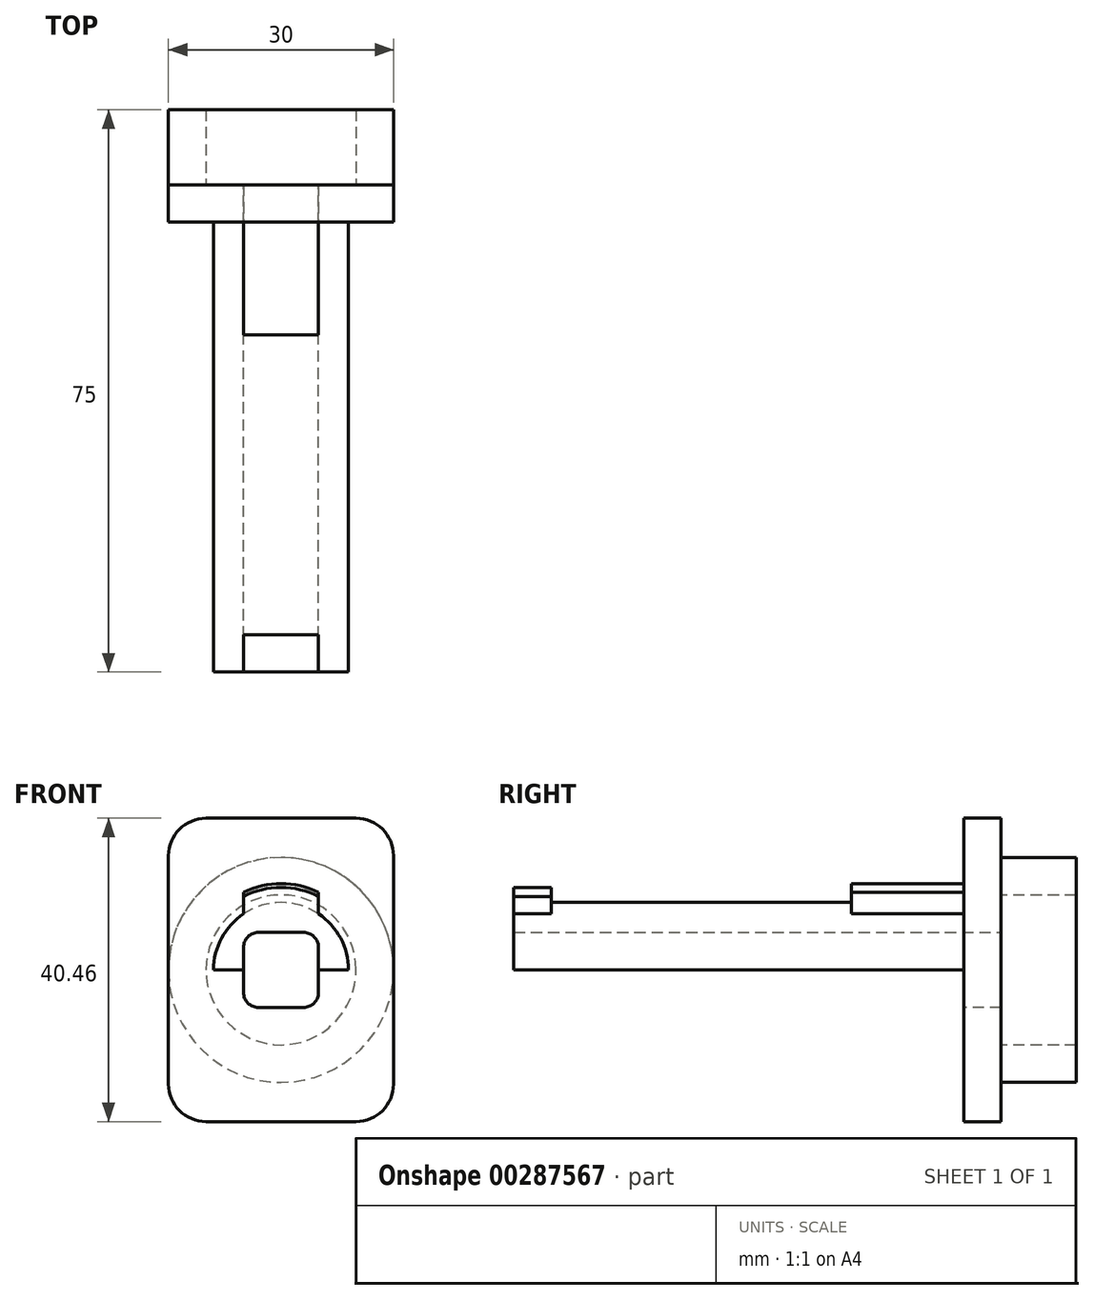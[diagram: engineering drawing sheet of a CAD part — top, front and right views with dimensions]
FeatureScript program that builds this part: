
annotation { "Feature Type Name" : "Feature", "Feature Type Description" : "" }
export const myFeature = defineFeature(function(context is Context, id is Id, definition is map)
    precondition{}
    {
        {
            var Q0;
            Q0=qCreatedBy(makeId("Front.planeOp"),FACE);
            var sketch = newSketch(context, id + "F0", { "sketchPlane" : qUnion([Q0])});
            skArc(sketch, "E0", {"start": v(9, 0) * mm, "mid": v(0, 9) * mm, "end": v(-9, 0) * mm});
            skLineSegment(sketch, "E1.bottom", {"start": v(10, -20.23) * mm, "end": v(-10, -20.23) * mm});
            skLineSegment(sketch, "E1.top", {"start": v(10, 20.23) * mm, "end": v(-10, 20.23) * mm});
            skLineSegment(sketch, "E1.left", {"start": v(15, -15.23) * mm, "end": v(15, 15.23) * mm});
            skLineSegment(sketch, "E1.right", {"start": v(-15, -15.23) * mm, "end": v(-15, 15.23) * mm});
            skPoint(sketch, "E2.visualSharp", {"position": v(-15, 20.23) * mm});
            skArc(sketch, "E2.filletArc", {"start": v(-10, 20.23) * mm, "mid": v(-13.54, 18.77) * mm, "end": v(-15, 15.23) * mm});
            skPoint(sketch, "E3.visualSharp", {"position": v(15, 20.23) * mm});
            skArc(sketch, "E3.filletArc", {"start": v(15, 15.23) * mm, "mid": v(13.54, 18.77) * mm, "end": v(10, 20.23) * mm});
            skPoint(sketch, "E4.visualSharp", {"position": v(15, -20.23) * mm});
            skArc(sketch, "E4.filletArc", {"start": v(10, -20.23) * mm, "mid": v(13.54, -18.77) * mm, "end": v(15, -15.23) * mm});
            skPoint(sketch, "E5.visualSharp", {"position": v(-15, -20.23) * mm});
            skArc(sketch, "E5.filletArc", {"start": v(-15, -15.23) * mm, "mid": v(-13.54, -18.77) * mm, "end": v(-10, -20.23) * mm});
            skLineSegment(sketch, "E6", {"start": v(-9, 0) * mm, "end": v(9, 0) * mm});
            skLineSegment(sketch, "E7.bottom", {"start": v(3, 5) * mm, "end": v(-3, 5) * mm});
            skLineSegment(sketch, "E7.top", {"start": v(3, -5) * mm, "end": v(-3, -5) * mm});
            skLineSegment(sketch, "E7.left", {"start": v(5, 3) * mm, "end": v(5, -3) * mm});
            skLineSegment(sketch, "E7.right", {"start": v(-5, 3) * mm, "end": v(-5, -3) * mm});
            skPoint(sketch, "E8.visualSharp", {"position": v(-5, 5) * mm});
            skArc(sketch, "E8.filletArc", {"start": v(-3, 5) * mm, "mid": v(-4.41, 4.41) * mm, "end": v(-5, 3) * mm});
            skPoint(sketch, "E9.visualSharp", {"position": v(5, 5) * mm});
            skArc(sketch, "E9.filletArc", {"start": v(5, 3) * mm, "mid": v(4.41, 4.41) * mm, "end": v(3, 5) * mm});
            skPoint(sketch, "E10.visualSharp", {"position": v(-5, -5) * mm});
            skArc(sketch, "E10.filletArc", {"start": v(-5, -3) * mm, "mid": v(-4.41, -4.41) * mm, "end": v(-3, -5) * mm});
            skPoint(sketch, "E11.visualSharp", {"position": v(5, -5) * mm});
            skArc(sketch, "E11.filletArc", {"start": v(3, -5) * mm, "mid": v(4.41, -4.41) * mm, "end": v(5, -3) * mm});
            skArc(sketch, "E12", {"start": v(5, 10.36) * mm, "mid": v(0, 11.5) * mm, "end": v(-5, 10.36) * mm});
            skLineSegment(sketch, "E13", {"start": v(-5, 3) * mm, "end": v(-5, 10.36) * mm});
            skLineSegment(sketch, "E14", {"start": v(5, 3) * mm, "end": v(5, 10.36) * mm});
            skSolve(sketch);
        }
        {
            var Q0;
            Q0=makeQuery(id+"F0.imprint","IMPRINT",FACE,{"disambiguationData":[TD([[makeQuery(id+"F0.imprint","IMPRINT",EDGE,{"derivedFrom":sQuery(id+"F0.wireOp",EDGE,"E0")}),1.0]])]});
            var Q1;
            Q1=makeQuery(id+"F0.imprint","IMPRINT",FACE,{"disambiguationData":[TD([[makeQuery(id+"F0.imprint","IMPRINT",EDGE,{"derivedFrom":sQuery(id+"F0.wireOp",EDGE,"E7.bottom")}),-1.0]])]});
            extrude(context, id + "F1", {"entities" : qUnion([Q0, Q1]), "depth" : 55 * mm});
        }
        {
            var Q0;
            Q0=makeQuery(id+"F1.opExtrude","CAP_FACE",FACE,{"disambiguationData":[OSD([sQuery(id+"F0.wireOp",EDGE,"E0"),sQuery(id+"F0.wireOp",EDGE,"E6"),sQuery(id+"F0.wireOp",EDGE,"E7.bottom"),sQuery(id+"F0.wireOp",EDGE,"E7.left"),sQuery(id+"F0.wireOp",EDGE,"E7.right"),sQuery(id+"F0.wireOp",EDGE,"E8.filletArc"),sQuery(id+"F0.wireOp",EDGE,"E9.filletArc")])],"isStart":false});
            var sketch = newSketch(context, id + "F2", { "sketchPlane" : qUnion([Q0])});
            skLineSegment(sketch, "E15.bottom", {"start": v(-5, 3) * mm, "end": v(5, 3) * mm});
            skLineSegment(sketch, "E15.left", {"start": v(-5, 3) * mm, "end": v(-5, 9.8) * mm});
            skLineSegment(sketch, "E15.right", {"start": v(5, 3) * mm, "end": v(5, 9.8) * mm});
            skArc(sketch, "E16", {"start": v(5, 9.8) * mm, "mid": v(0, 11) * mm, "end": v(-5, 9.8) * mm});
            skPoint(sketch, "E15.top.end.orphan", {"position": v(5, 11) * mm});
            skSolve(sketch);
        }
        {
            var Q0;
            {var subQ1=sQuery(id+"F0.wireOp",EDGE,"E7.right");var subQ2=makeQuery(id+"F1.opExtrude","CAP_EDGE",EDGE,{"disambiguationData":[OSD([subQ1])],"isStart":false});Q0=makeQuery(id+"F2.imprint","IMPRINT",FACE,{"disambiguationData":[TD([[makeQuery(id+"F2.imprint","IMPRINT",EDGE,{"derivedFrom":subQ2}),-1.0]])]});}
            var Q1;
            Q1=makeQuery(id+"F2.imprint","IMPRINT",FACE,{"disambiguationData":[TD([[makeQuery(id+"F2.imprint","IMPRINT",EDGE,{"derivedFrom":makeQuery(id+"F1.opExtrude","CAP_EDGE",EDGE,{"disambiguationData":[OSD([sQuery(id+"F0.wireOp",EDGE,"E7.bottom")])],"isStart":false})}),-1.0]])]});
            var Q2;
            {var subQ0=sQuery(id+"F2.wireOp",EDGE,"E16");Q2=makeQuery(id+"F2.imprint","IMPRINT",FACE,{"disambiguationData":[TD([[makeQuery(id+"F2.imprint","IMPRINT",EDGE,{"derivedFrom":subQ0}),1.0]])]});}
            var Q3;
            {var subQ1=sQuery(id+"F0.wireOp",EDGE,"E7.left");var subQ2=makeQuery(id+"F1.opExtrude","CAP_EDGE",EDGE,{"disambiguationData":[OSD([subQ1])],"isStart":false});Q3=makeQuery(id+"F2.imprint","IMPRINT",FACE,{"disambiguationData":[TD([[makeQuery(id+"F2.imprint","IMPRINT",EDGE,{"derivedFrom":subQ2}),1.0]])]});}
            extrude(context, id + "F3", {"entities" : qUnion([Q0, Q1, Q2, Q3]), "operationType" : NewBodyOperationType.ADD, "depth" : 5 * mm});
        }
        {
            var Q0;
            Q0 = qSketchRegion(id + "F0", true);
            var Q1;
            {var subQ0=sQuery(id+"F0.wireOp",EDGE,"E6");var subQ1=sQuery(id+"F0.wireOp",EDGE,"E0");var subQ2=makeQuery(id+"F0.imprint","INTERSECT",VERTEX,{"disambiguationData":[OD(0.0)],"derivedFrom":[subQ1,subQ0]});Q1=makeQuery(id+"F0.imprint","IMPRINT",FACE,{"disambiguationData":[TD([[makeQuery(id+"F0.imprint","IMPRINT",EDGE,{"disambiguationData":[TD([[subQ2,-1.0]])],"derivedFrom":subQ1}),1.0]])]});}
            var Q2;
            Q2=makeQuery(id+"F0.imprint","IMPRINT",FACE,{"disambiguationData":[TD([[makeQuery(id+"F0.imprint","IMPRINT",EDGE,{"derivedFrom":sQuery(id+"F0.wireOp",EDGE,"E7.bottom")}),-1.0]])]});
            var Q3;
            {var subQ0=sQuery(id+"F0.wireOp",EDGE,"E6");var subQ1=sQuery(id+"F0.wireOp",EDGE,"E0");var subQ2=makeQuery(id+"F0.imprint","INTERSECT",VERTEX,{"disambiguationData":[OD(1.0)],"derivedFrom":[subQ1,subQ0]});Q3=makeQuery(id+"F0.imprint","IMPRINT",FACE,{"disambiguationData":[TD([[makeQuery(id+"F0.imprint","IMPRINT",EDGE,{"disambiguationData":[TD([[subQ2,1.0]])],"derivedFrom":subQ1}),1.0]])]});}
            var Q4;
            {var subQ5=sQuery(id+"F0.wireOp",EDGE,"E12");Q4=makeQuery(id+"F0.imprint","IMPRINT",FACE,{"disambiguationData":[TD([[makeQuery(id+"F0.imprint","IMPRINT",EDGE,{"derivedFrom":subQ5}),1.0]])]});}
            extrude(context, id + "F4", {"entities" : qUnion([Q0, Q1, Q2, Q3, Q4]), "oppositeDirection" : true, "depth" : 5 * mm});
        }
        {
            var Q0;
            Q0=makeQuery(id+"F4.opExtrude","CAP_FACE",FACE,{"disambiguationData":[OSD([sQuery(id+"F0.wireOp",EDGE,"E0"),sQuery(id+"F0.wireOp",EDGE,"E1.bottom"),sQuery(id+"F0.wireOp",EDGE,"E1.top"),sQuery(id+"F0.wireOp",EDGE,"E1.left"),sQuery(id+"F0.wireOp",EDGE,"E1.right"),sQuery(id+"F0.wireOp",EDGE,"E2.filletArc"),sQuery(id+"F0.wireOp",EDGE,"E3.filletArc"),sQuery(id+"F0.wireOp",EDGE,"E4.filletArc"),sQuery(id+"F0.wireOp",EDGE,"E5.filletArc")])],"isStart":false});
            var sketch = newSketch(context, id + "F5", { "sketchPlane" : qUnion([Q0])});
            skCircle(sketch, "E17", {"center": v(0, 0) * mm, "radius": 15 * mm});
            skCircle(sketch, "E18", {"center": v(0, 0) * mm, "radius": 10 * mm});
            skSolve(sketch);
        }
        {
            var Q0;
            Q0=makeQuery(id+"F5.imprint","IMPRINT",FACE,{"disambiguationData":[TD([[makeQuery(id+"F5.imprint","IMPRINT",EDGE,{"derivedFrom":sQuery(id+"F5.wireOp",EDGE,"E18")}),-1.0]])]});
            extrude(context, id + "F6", {"entities" : qUnion([Q0]), "operationType" : NewBodyOperationType.ADD, "depth" : 10 * mm});
        }
        {
            var Q0;
            {var subQ5=sQuery(id+"F0.wireOp",EDGE,"E12");Q0=makeQuery(id+"F0.imprint","IMPRINT",FACE,{"disambiguationData":[TD([[makeQuery(id+"F0.imprint","IMPRINT",EDGE,{"derivedFrom":subQ5}),1.0]])]});}
            extrude(context, id + "F7", {"entities" : qUnion([Q0]), "operationType" : NewBodyOperationType.ADD, "depth" : 15 * mm});
        }
    });
